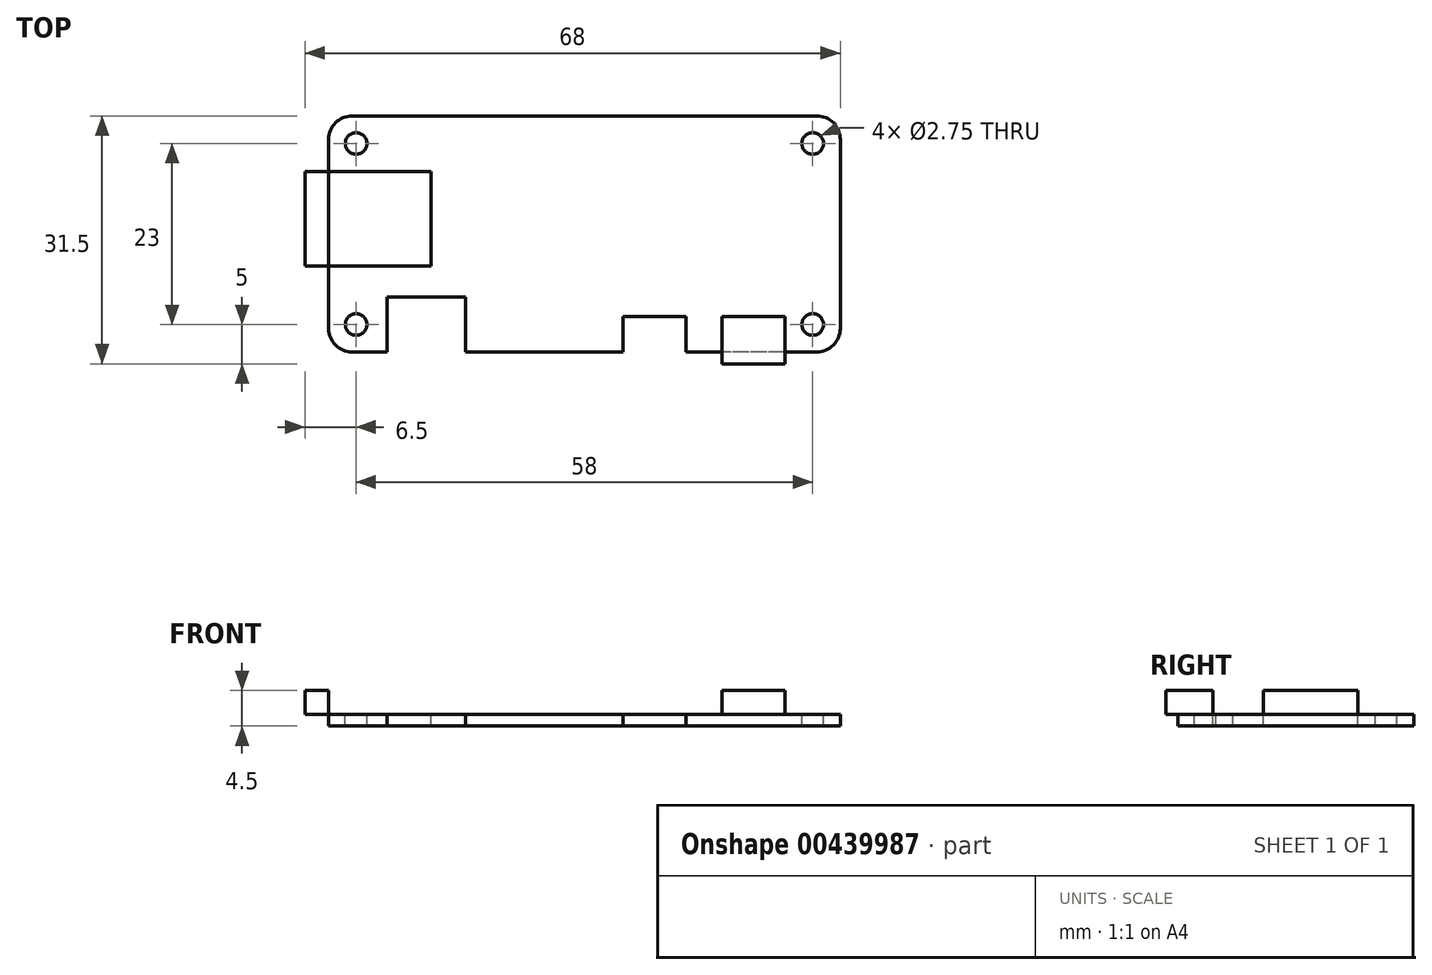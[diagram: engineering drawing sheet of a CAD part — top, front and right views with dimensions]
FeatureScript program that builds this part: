
annotation { "Feature Type Name" : "Feature", "Feature Type Description" : "" }
export const myFeature = defineFeature(function(context is Context, id is Id, definition is map)
    precondition{}
    {
        {
            var Q0;
            Q0=qCreatedBy(makeId("Top.planeOp"),FACE);
            var sketch = newSketch(context, id + "F0", { "sketchPlane" : qUnion([Q0])});
            skLineSegment(sketch, "E0.bottom", {"start": v(-3, 0) * mm, "end": v(-62, 0) * mm});
            skLineSegment(sketch, "E0.top", {"start": v(-3, 30) * mm, "end": v(-62, 30) * mm});
            skLineSegment(sketch, "E0.left", {"start": v(0, 3) * mm, "end": v(0, 27) * mm});
            skLineSegment(sketch, "E0.right", {"start": v(-65, 3) * mm, "end": v(-65, 27) * mm});
            skPoint(sketch, "E1.visualSharp", {"position": v(-65, 30) * mm});
            skArc(sketch, "E1.filletArc", {"start": v(-62, 30) * mm, "mid": v(-64.12, 29.12) * mm, "end": v(-65, 27) * mm});
            skPoint(sketch, "E2.visualSharp", {"position": v(0, 30) * mm});
            skArc(sketch, "E2.filletArc", {"start": v(0, 27) * mm, "mid": v(-0.88, 29.12) * mm, "end": v(-3, 30) * mm});
            skPoint(sketch, "E3.visualSharp", {"position": v(-65, 0) * mm});
            skArc(sketch, "E3.filletArc", {"start": v(-65, 3) * mm, "mid": v(-64.12, 0.88) * mm, "end": v(-62, 0) * mm});
            skPoint(sketch, "E4.visualSharp", {"position": v(0, 0) * mm});
            skArc(sketch, "E4.filletArc", {"start": v(-3, 0) * mm, "mid": v(-0.88, 0.88) * mm, "end": v(0, 3) * mm});
            skPoint(sketch, "E5", {"position": v(-61.5, 26.5) * mm});
            skPoint(sketch, "E6", {"position": v(-3.5, 26.5) * mm});
            skPoint(sketch, "E7", {"position": v(-61.5, 3.5) * mm});
            skPoint(sketch, "E8", {"position": v(-3.5, 3.5) * mm});
            skCircle(sketch, "E9", {"center": v(-3.5, 26.5) * mm, "radius": 1.38 * mm});
            skCircle(sketch, "E10", {"center": v(-61.5, 26.5) * mm, "radius": 1.38 * mm});
            skCircle(sketch, "E11", {"center": v(-61.5, 3.5) * mm, "radius": 1.38 * mm});
            skCircle(sketch, "E12", {"center": v(-3.5, 3.5) * mm, "radius": 1.38 * mm});
            skPoint(sketch, "E13", {"position": v(-65, 16.9) * mm});
            skPoint(sketch, "E14", {"position": v(-65, 22.9) * mm});
            skLineSegment(sketch, "E15.bottom", {"start": v(-65, 22.9) * mm, "end": v(-68, 22.9) * mm});
            skLineSegment(sketch, "E15.top", {"start": v(-65, 10.9) * mm, "end": v(-68, 10.9) * mm});
            skLineSegment(sketch, "E15.left", {"start": v(-65, 22.9) * mm, "end": v(-65, 10.9) * mm});
            skLineSegment(sketch, "E15.right", {"start": v(-68, 22.9) * mm, "end": v(-68, 10.9) * mm});
            skPoint(sketch, "E16", {"position": v(-52.6, 0) * mm});
            skPoint(sketch, "E17", {"position": v(-23.6, 0) * mm});
            skPoint(sketch, "E18", {"position": v(-11, 0) * mm});
            skPoint(sketch, "E19", {"position": v(-52, 22.9) * mm});
            skPoint(sketch, "E20", {"position": v(-52, 10.9) * mm});
            skLineSegment(sketch, "E21", {"start": v(-65, 22.9) * mm, "end": v(-52, 22.9) * mm});
            skLineSegment(sketch, "E22", {"start": v(-52, 10.9) * mm, "end": v(-52, 22.9) * mm});
            skLineSegment(sketch, "E23", {"start": v(-52, 10.9) * mm, "end": v(-65, 10.9) * mm});
            skPoint(sketch, "E24", {"position": v(-57.6, 0) * mm});
            skLineSegment(sketch, "E25.bottom", {"start": v(-57.6, 0) * mm, "end": v(-47.6, 0) * mm});
            skLineSegment(sketch, "E25.top", {"start": v(-57.6, -1) * mm, "end": v(-47.6, -1) * mm});
            skLineSegment(sketch, "E25.left", {"start": v(-57.6, 0) * mm, "end": v(-57.6, -1) * mm});
            skLineSegment(sketch, "E25.right", {"start": v(-47.6, 0) * mm, "end": v(-47.6, -1) * mm});
            skPoint(sketch, "E26", {"position": v(-57.6, 7) * mm});
            skPoint(sketch, "E27", {"position": v(-47.6, 7) * mm});
            skLineSegment(sketch, "E28", {"start": v(-57.6, 0) * mm, "end": v(-57.6, 7) * mm});
            skLineSegment(sketch, "E29", {"start": v(-47.6, 7) * mm, "end": v(-47.6, 0) * mm});
            skLineSegment(sketch, "E30", {"start": v(-47.6, 7) * mm, "end": v(-57.6, 7) * mm});
            skPoint(sketch, "E31", {"position": v(-27.6, 0) * mm});
            skLineSegment(sketch, "E32.bottom", {"start": v(-27.6, 0) * mm, "end": v(-19.6, 0) * mm});
            skLineSegment(sketch, "E32.top", {"start": v(-27.6, 4.5) * mm, "end": v(-19.6, 4.5) * mm});
            skLineSegment(sketch, "E32.left", {"start": v(-27.6, 0) * mm, "end": v(-27.6, 4.5) * mm});
            skLineSegment(sketch, "E32.right", {"start": v(-19.6, 0) * mm, "end": v(-19.6, 4.5) * mm});
            skPoint(sketch, "E33", {"position": v(-27.6, -1.5) * mm});
            skPoint(sketch, "E34", {"position": v(-19.6, -1.5) * mm});
            skLineSegment(sketch, "E35", {"start": v(-27.6, 0) * mm, "end": v(-27.6, -1.5) * mm});
            skLineSegment(sketch, "E36", {"start": v(-19.6, -1.5) * mm, "end": v(-27.6, -1.5) * mm});
            skLineSegment(sketch, "E37", {"start": v(-19.6, -1.5) * mm, "end": v(-19.6, 0) * mm});
            skPoint(sketch, "E38", {"position": v(-15, 0) * mm});
            skPoint(sketch, "E39", {"position": v(-15, 4.5) * mm});
            skPoint(sketch, "E40", {"position": v(-7, 0) * mm});
            skPoint(sketch, "E41", {"position": v(-7, 4.5) * mm});
            skPoint(sketch, "E42", {"position": v(-15, -1.5) * mm});
            skPoint(sketch, "E43", {"position": v(-7, -1.5) * mm});
            skLineSegment(sketch, "E44", {"start": v(-15, 0) * mm, "end": v(-15, 4.5) * mm});
            skLineSegment(sketch, "E45", {"start": v(-7, 4.5) * mm, "end": v(-7, 0) * mm});
            skLineSegment(sketch, "E46", {"start": v(-7, 4.5) * mm, "end": v(-15, 4.5) * mm});
            skLineSegment(sketch, "E47", {"start": v(-15, 0) * mm, "end": v(-15, -1.5) * mm});
            skLineSegment(sketch, "E48", {"start": v(-15, -1.5) * mm, "end": v(-7, -1.5) * mm});
            skLineSegment(sketch, "E49", {"start": v(-7, -1.5) * mm, "end": v(-7, 0) * mm});
            skSolve(sketch);
        }
        {
            var Q0;
            Q0=makeQuery(id+"F0.imprint","IMPRINT",FACE,{"disambiguationData":[TD([[makeQuery(id+"F0.imprint","IMPRINT",EDGE,{"derivedFrom":sQuery(id+"F0.wireOp",EDGE,"E0.top")}),1.0]])]});
            var Q1;
            Q1=makeQuery(id+"F0.imprint","IMPRINT",FACE,{"disambiguationData":[TD([[makeQuery(id+"F0.imprint","IMPRINT",EDGE,{"derivedFrom":sQuery(id+"F0.wireOp",EDGE,"E25.bottom")}),1.0]])]});
            var Q2;
            Q2=makeQuery(id+"F0.imprint","IMPRINT",FACE,{"disambiguationData":[TD([[makeQuery(id+"F0.imprint","IMPRINT",EDGE,{"derivedFrom":sQuery(id+"F0.wireOp",EDGE,"E15.left")}),1.0]])]});
            var Q3;
            Q3=makeQuery(id+"F0.imprint","IMPRINT",FACE,{"disambiguationData":[TD([[makeQuery(id+"F0.imprint","IMPRINT",EDGE,{"derivedFrom":sQuery(id+"F0.wireOp",EDGE,"E32.bottom")}),1.0]])]});
            var Q4;
            {var subQ0=sQuery(id+"F0.wireOp",EDGE,"E44");Q4=makeQuery(id+"F0.imprint","IMPRINT",FACE,{"disambiguationData":[TD([[makeQuery(id+"F0.imprint","IMPRINT",EDGE,{"derivedFrom":subQ0}),-1.0]])]});}
            extrude(context, id + "F1", {"entities" : qUnion([Q0, Q1, Q2, Q3, Q4]), "oppositeDirection" : true, "depth" : 1.5 * mm});
        }
        {
            var Q0;
            Q0=makeQuery(id+"F0.imprint","IMPRINT",FACE,{"disambiguationData":[TD([[makeQuery(id+"F0.imprint","IMPRINT",EDGE,{"derivedFrom":sQuery(id+"F0.wireOp",EDGE,"E15.left")}),1.0]])]});
            var Q1;
            Q1=makeQuery(id+"F0.imprint","IMPRINT",FACE,{"disambiguationData":[TD([[makeQuery(id+"F0.imprint","IMPRINT",EDGE,{"derivedFrom":sQuery(id+"F0.wireOp",EDGE,"E15.bottom")}),1.0]])]});
            var Q2;
            Q2=makeQuery(id+"F0.imprint","IMPRINT",FACE,{"disambiguationData":[TD([[makeQuery(id+"F0.imprint","IMPRINT",EDGE,{"derivedFrom":sQuery(id+"F0.wireOp",EDGE,"E25.bottom")}),1.0]])]});
            var Q3;
            Q3=makeQuery(id+"F0.imprint","IMPRINT",FACE,{"disambiguationData":[TD([[makeQuery(id+"F0.imprint","IMPRINT",EDGE,{"derivedFrom":sQuery(id+"F0.wireOp",EDGE,"E25.bottom")}),-1.0]])]});
            var Q4;
            Q4=makeQuery(id+"F0.imprint","IMPRINT",FACE,{"disambiguationData":[TD([[makeQuery(id+"F0.imprint","IMPRINT",EDGE,{"derivedFrom":sQuery(id+"F0.wireOp",EDGE,"E32.bottom")}),1.0]])]});
            var Q5;
            Q5=makeQuery(id+"F0.imprint","IMPRINT",FACE,{"disambiguationData":[TD([[makeQuery(id+"F0.imprint","IMPRINT",EDGE,{"derivedFrom":sQuery(id+"F0.wireOp",EDGE,"E32.bottom")}),-1.0]])]});
            var Q6;
            {var subQ0=sQuery(id+"F0.wireOp",EDGE,"E44");Q6=makeQuery(id+"F0.imprint","IMPRINT",FACE,{"disambiguationData":[TD([[makeQuery(id+"F0.imprint","IMPRINT",EDGE,{"derivedFrom":subQ0}),-1.0]])]});}
            var Q7;
            {var subQ0=sQuery(id+"F0.wireOp",EDGE,"E47");Q7=makeQuery(id+"F0.imprint","IMPRINT",FACE,{"disambiguationData":[TD([[makeQuery(id+"F0.imprint","IMPRINT",EDGE,{"derivedFrom":subQ0}),1.0]])]});}
            extrude(context, id + "F2", {"entities" : qUnion([Q0, Q1, Q2, Q3, Q4, Q5, Q6, Q7]), "operationType" : NewBodyOperationType.ADD, "depth" : 3 * mm});
        }
    });
